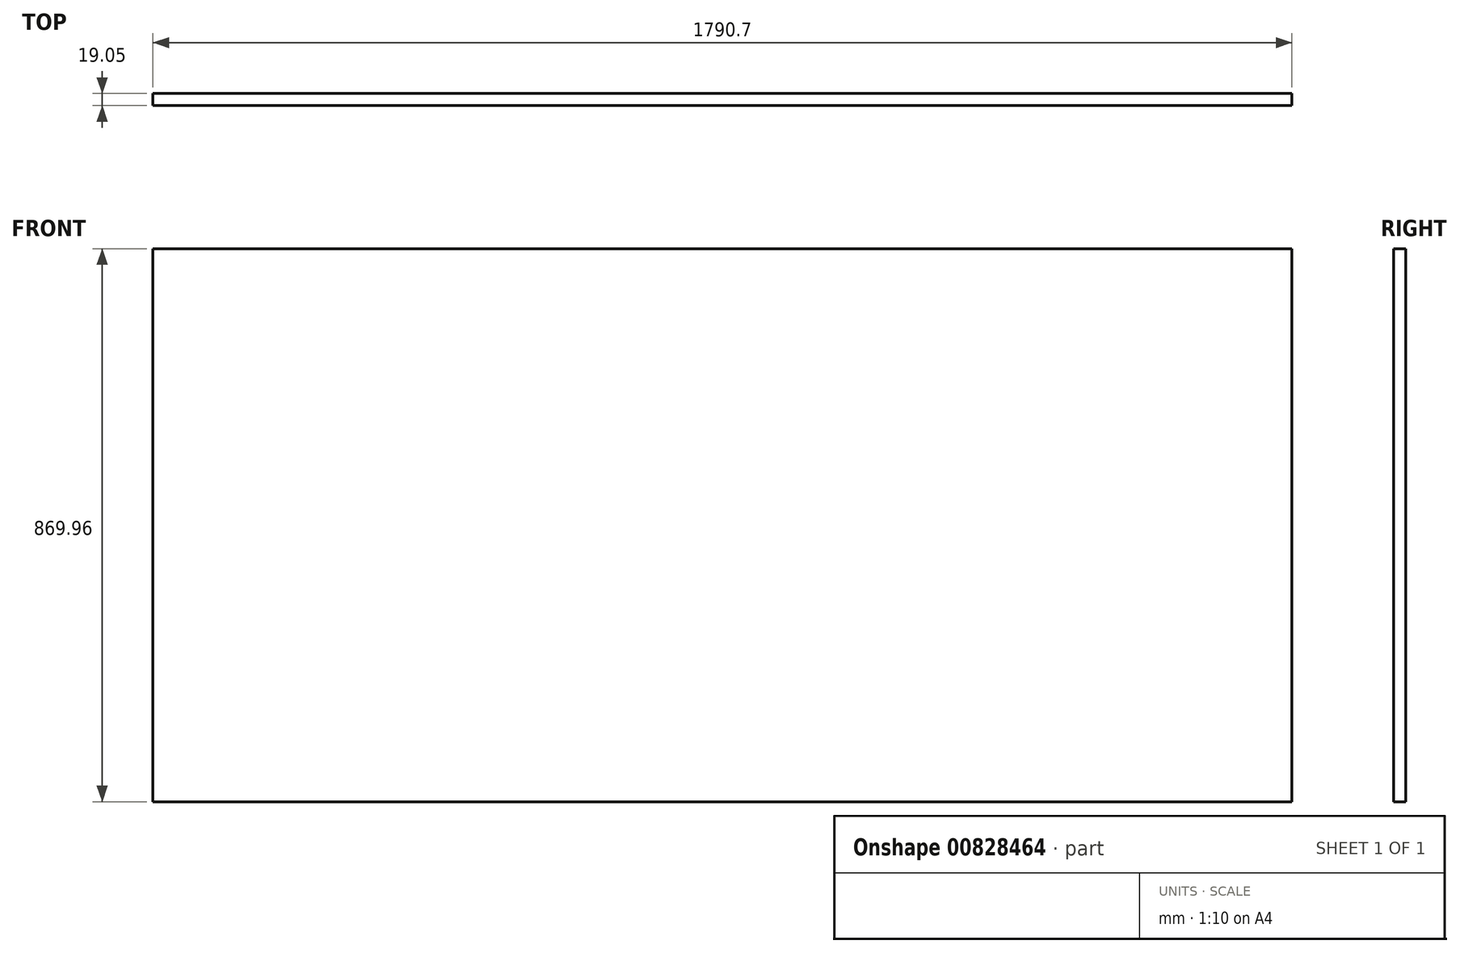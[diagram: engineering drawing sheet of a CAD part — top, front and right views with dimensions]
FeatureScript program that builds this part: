
annotation { "Feature Type Name" : "Feature", "Feature Type Description" : "" }
export const myFeature = defineFeature(function(context is Context, id is Id, definition is map)
    precondition{}
    {
        {
            var Q0;
            Q0=qCreatedBy(makeId("Front.planeOp"),FACE);
            var sketch = newSketch(context, id + "F0", { "sketchPlane" : qUnion([Q0])});
            skLineSegment(sketch, "E0.bottom", {"start": v(-895.35, 434.98) * mm, "end": v(895.35, 434.98) * mm});
            skLineSegment(sketch, "E0.top", {"start": v(-895.35, -434.98) * mm, "end": v(895.35, -434.98) * mm});
            skLineSegment(sketch, "E0.left", {"start": v(-895.35, 434.98) * mm, "end": v(-895.35, -434.98) * mm});
            skLineSegment(sketch, "E0.right", {"start": v(895.35, 434.98) * mm, "end": v(895.35, -434.98) * mm});
            skPoint(sketch, "E0.middle", {"position": v(0, 0) * mm});
            skSolve(sketch);
        }
        {
            var Q0;
            Q0=makeQuery(id+"F0.imprint","IMPRINT",FACE,{"disambiguationData":[TD([[makeQuery(id+"F0.imprint","IMPRINT",EDGE,{"derivedFrom":sQuery(id+"F0.wireOp",EDGE,"E0.bottom")}),-1.0]])]});
            extrude(context, id + "F1", {"entities" : qUnion([Q0]), "depth" : 19.05 * mm, "offsetDistance" : 25.4 * mm});
        }
    });
